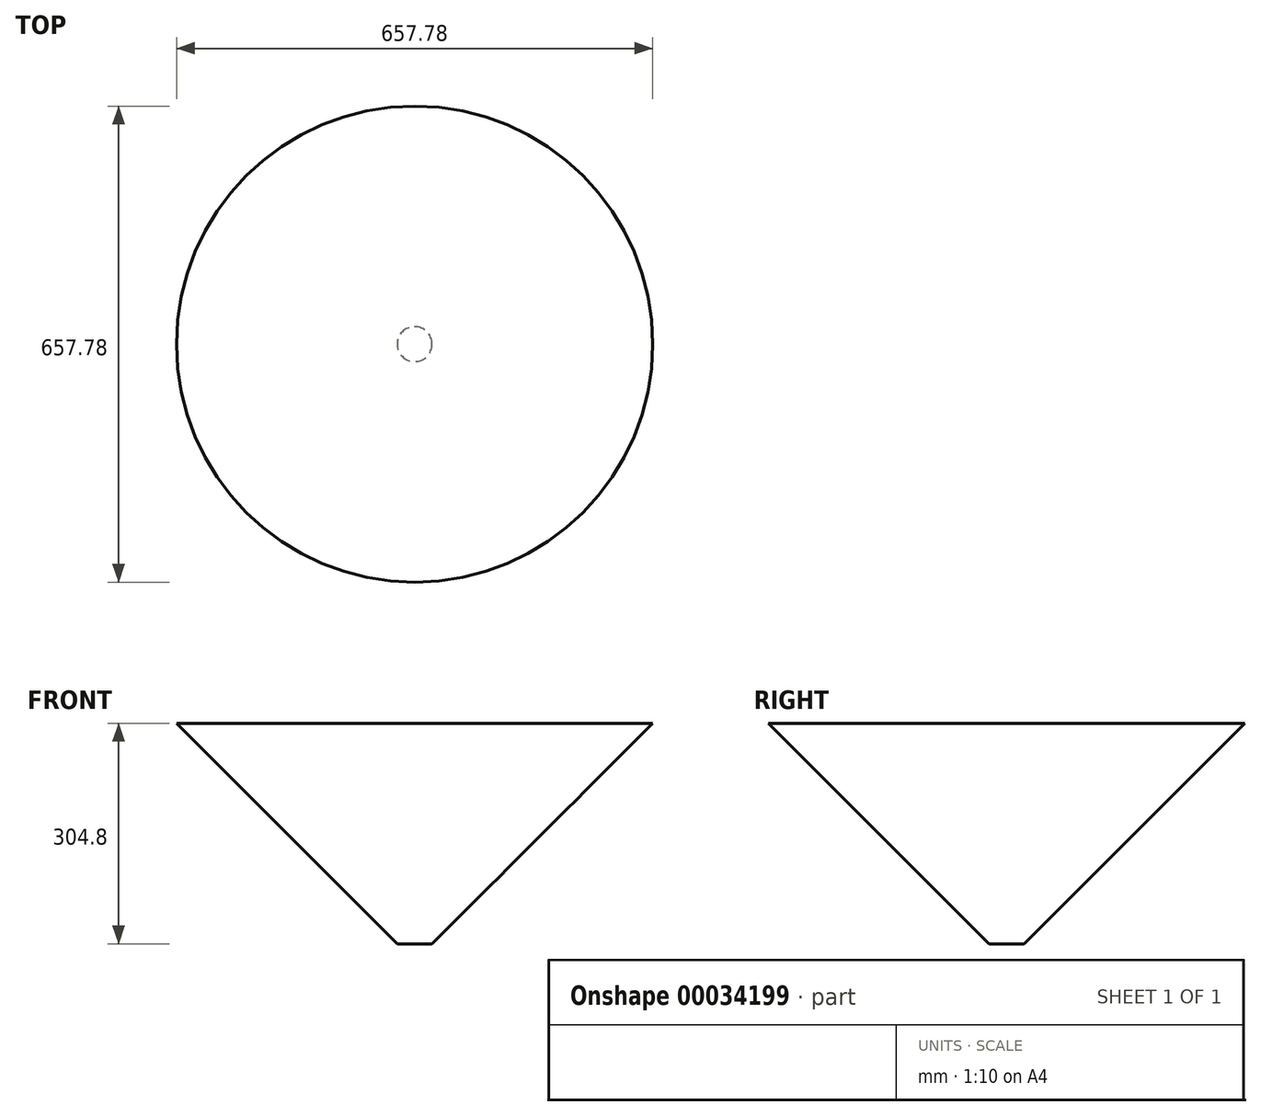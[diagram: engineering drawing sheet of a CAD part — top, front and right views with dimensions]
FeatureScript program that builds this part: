
annotation { "Feature Type Name" : "Feature", "Feature Type Description" : "" }
export const myFeature = defineFeature(function(context is Context, id is Id, definition is map)
    precondition{}
    {
        {
            var Q0;
            Q0=qCreatedBy(makeId("Top.planeOp"),FACE);
            var sketch = newSketch(context, id + "F0", { "sketchPlane" : qUnion([Q0])});
            skCircle(sketch, "E0", {"center": v(-92.9, 0) * mm, "radius": 24.1 * mm});
            skSolve(sketch);
        }
        {
            var Q0;
            Q0=makeQuery(id+"F0.imprint","IMPRINT",FACE,{"disambiguationData":[TD([[makeQuery(id+"F0.imprint","IMPRINT",EDGE,{"derivedFrom":sQuery(id+"F0.wireOp",EDGE,"E0")}),1.0]])]});
            extrude(context, id + "F1", {"entities" : qUnion([Q0]), "depth" : 304.8 * mm, "hasDraft" : true, "draftAngle" : 45 * degree});
        }
    });
